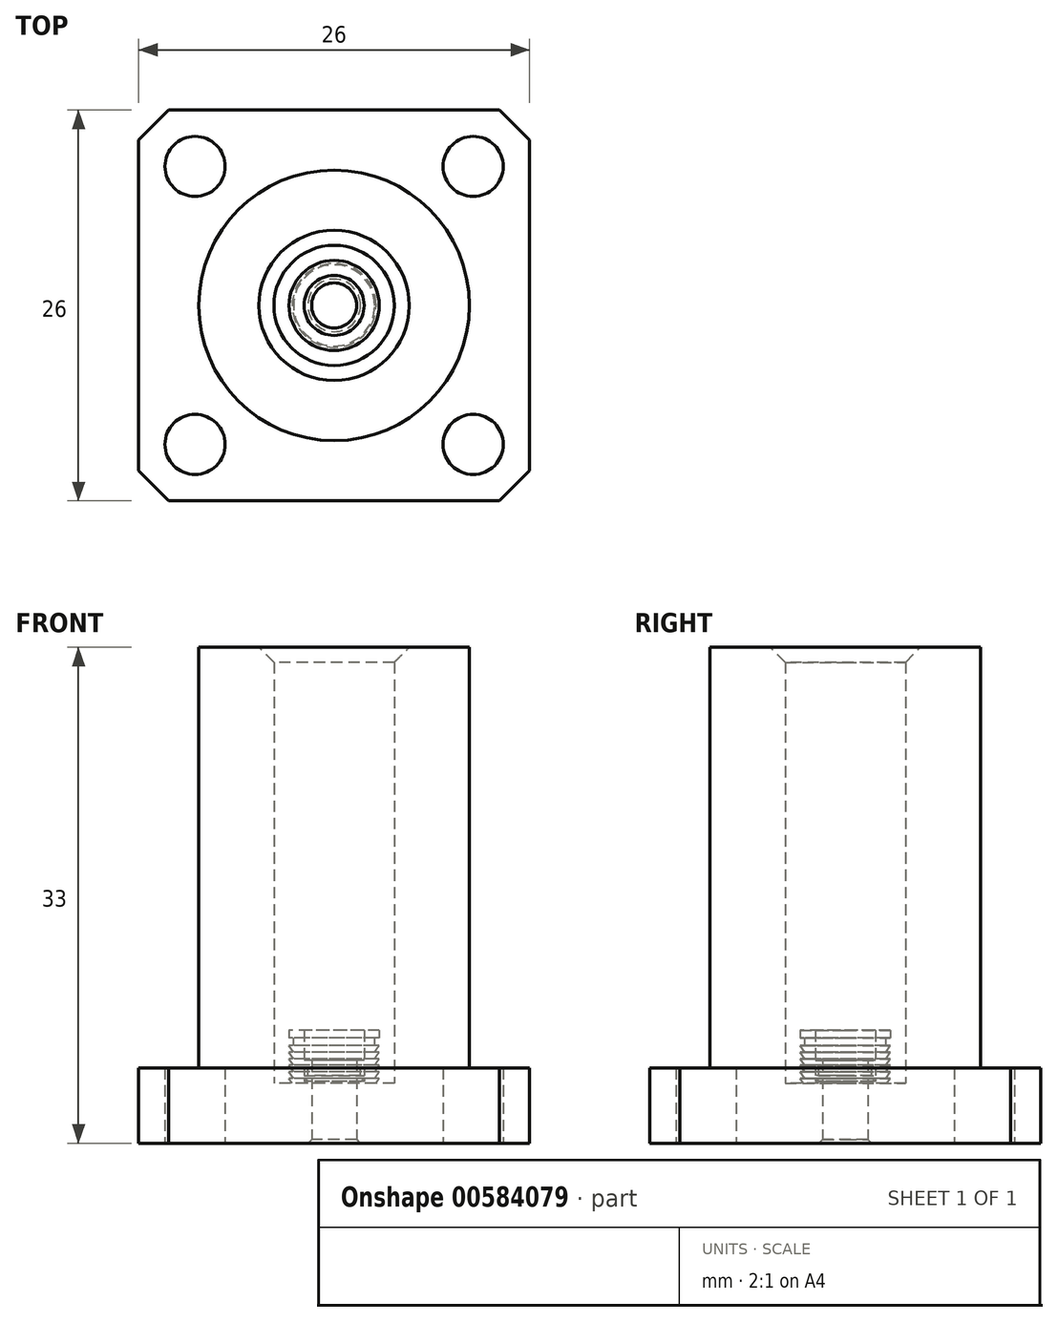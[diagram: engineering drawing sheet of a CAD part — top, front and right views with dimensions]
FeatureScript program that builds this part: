
annotation { "Feature Type Name" : "Feature", "Feature Type Description" : "" }
export const myFeature = defineFeature(function(context is Context, id is Id, definition is map)
    precondition{}
    {
        {
            var Q0;
            Q0=qCreatedBy(makeId("Top.planeOp"),FACE);
            var sketch = newSketch(context, id + "F0", { "sketchPlane" : qUnion([Q0])});
            skCircle(sketch, "E0", {"center": v(0, 0) * mm, "radius": 2.25 * mm});
            skCircle(sketch, "E1", {"center": v(0, 0) * mm, "radius": 1.5 * mm});
            skSolve(sketch);
        }
        {
            var Q0;
            Q0=makeQuery(id+"F0.imprint","IMPRINT",FACE,{"disambiguationData":[TD([[makeQuery(id+"F0.imprint","IMPRINT",EDGE,{"derivedFrom":sQuery(id+"F0.wireOp",EDGE,"E0")}),1.0]])]});
            extrude(context, id + "F1", {"entities" : qUnion([Q0]), "depth" : 5.5 * mm, "offsetDistance" : 25 * mm});
        }
        {
            var Q0;
            Q0=qCreatedBy(makeId("Front.planeOp"),FACE);
            var sketch = newSketch(context, id + "F2", { "sketchPlane" : qUnion([Q0])});
            skLineSegment(sketch, "E2", {"start": v(-2.25, 0) * mm, "end": v(-2.25, 5.5) * mm});
            skLineSegment(sketch, "E3", {"start": v(2.25, 5.5) * mm, "end": v(2.25, 0) * mm});
            skLineSegment(sketch, "E4", {"start": v(2.25, 5) * mm, "end": v(1.75, 5) * mm});
            skLineSegment(sketch, "E5", {"start": v(1.75, 5) * mm, "end": v(1.75, 4.5) * mm});
            skLineSegment(sketch, "E6", {"start": v(1.75, 4.5) * mm, "end": v(2.25, 4.5) * mm});
            skLineSegment(sketch, "E7", {"start": v(2.25, 4.5) * mm, "end": v(1.75, 4.1) * mm});
            skLineSegment(sketch, "E8", {"start": v(1.75, 4.1) * mm, "end": v(2.25, 4.1) * mm});
            skLineSegment(sketch, "E9", {"start": v(2.25, 4.1) * mm, "end": v(1.75, 3.7) * mm});
            skLineSegment(sketch, "E10", {"start": v(1.75, 3.7) * mm, "end": v(2.25, 3.7) * mm});
            skLineSegment(sketch, "E11", {"start": v(2.25, 3.7) * mm, "end": v(1.75, 3.3) * mm});
            skLineSegment(sketch, "E12", {"start": v(1.75, 3.3) * mm, "end": v(2.25, 3.3) * mm});
            skPoint(sketch, "E12.endSnap0", {"position": v(2.25, 2.75) * mm});
            skLineSegment(sketch, "E13", {"start": v(2.25, 3.3) * mm, "end": v(1.75, 2.9) * mm});
            skLineSegment(sketch, "E14", {"start": v(1.75, 2.9) * mm, "end": v(2.25, 2.9) * mm});
            skLineSegment(sketch, "E15", {"start": v(2.25, 2.9) * mm, "end": v(1.75, 2.5) * mm});
            skLineSegment(sketch, "E16", {"start": v(1.75, 2.5) * mm, "end": v(2.25, 2.5) * mm});
            skLineSegment(sketch, "E17", {"start": v(2.25, 2.5) * mm, "end": v(1.75, 2.1) * mm});
            skLineSegment(sketch, "E18", {"start": v(1.75, 2.1) * mm, "end": v(2.25, 2.1) * mm});
            skLineSegment(sketch, "E19", {"start": v(2.25, 2.1) * mm, "end": v(1.75, 1.7) * mm});
            skLineSegment(sketch, "E20", {"start": v(1.75, 1.7) * mm, "end": v(2.25, 1.7) * mm});
            skLineSegment(sketch, "E21", {"start": v(2.25, 1.7) * mm, "end": v(1.75, 1.3) * mm});
            skLineSegment(sketch, "E22", {"start": v(1.75, 1.3) * mm, "end": v(2.25, 1.3) * mm});
            skLineSegment(sketch, "E23", {"start": v(2.25, 1.3) * mm, "end": v(1.75, 0.9) * mm});
            skLineSegment(sketch, "E24", {"start": v(1.75, 0.9) * mm, "end": v(1.75, 0.6) * mm});
            skLineSegment(sketch, "E25", {"start": v(1.75, 0.6) * mm, "end": v(2.25, 0.6) * mm});
            skLineSegment(sketch, "E26", {"start": v(2.25, 0.3) * mm, "end": v(1.95, 0) * mm});
            skLineSegment(sketch, "E27", {"start": v(2.25, 5) * mm, "end": v(2.25, 0) * mm});
            skLineSegment(sketch, "E28", {"start": v(1.95, 0) * mm, "end": v(2.25, 0) * mm});
            skSolve(sketch);
        }
        {
            var Q0;
            {var subQ0=sQuery(id+"F2.wireOp",EDGE,"E4");Q0=makeQuery(id+"F2.imprint","IMPRINT",FACE,{"disambiguationData":[TD([[makeQuery(id+"F2.imprint","IMPRINT",EDGE,{"derivedFrom":subQ0}),1.0]])]});}
            var Q1;
            {var subQ0=sQuery(id+"F2.wireOp",EDGE,"E7");Q1=makeQuery(id+"F2.imprint","IMPRINT",FACE,{"disambiguationData":[TD([[makeQuery(id+"F2.imprint","IMPRINT",EDGE,{"derivedFrom":subQ0}),1.0]])]});}
            var Q2;
            {var subQ0=sQuery(id+"F2.wireOp",EDGE,"E9");Q2=makeQuery(id+"F2.imprint","IMPRINT",FACE,{"disambiguationData":[TD([[makeQuery(id+"F2.imprint","IMPRINT",EDGE,{"derivedFrom":subQ0}),1.0]])]});}
            var Q3;
            {var subQ0=sQuery(id+"F2.wireOp",EDGE,"E11");Q3=makeQuery(id+"F2.imprint","IMPRINT",FACE,{"disambiguationData":[TD([[makeQuery(id+"F2.imprint","IMPRINT",EDGE,{"derivedFrom":subQ0}),1.0]])]});}
            var Q4;
            {var subQ0=sQuery(id+"F2.wireOp",EDGE,"E13");Q4=makeQuery(id+"F2.imprint","IMPRINT",FACE,{"disambiguationData":[TD([[makeQuery(id+"F2.imprint","IMPRINT",EDGE,{"derivedFrom":subQ0}),1.0]])]});}
            var Q5;
            {var subQ0=sQuery(id+"F2.wireOp",EDGE,"E15");Q5=makeQuery(id+"F2.imprint","IMPRINT",FACE,{"disambiguationData":[TD([[makeQuery(id+"F2.imprint","IMPRINT",EDGE,{"derivedFrom":subQ0}),1.0]])]});}
            var Q6;
            {var subQ0=sQuery(id+"F2.wireOp",EDGE,"E17");Q6=makeQuery(id+"F2.imprint","IMPRINT",FACE,{"disambiguationData":[TD([[makeQuery(id+"F2.imprint","IMPRINT",EDGE,{"derivedFrom":subQ0}),1.0]])]});}
            var Q7;
            {var subQ0=sQuery(id+"F2.wireOp",EDGE,"E19");Q7=makeQuery(id+"F2.imprint","IMPRINT",FACE,{"disambiguationData":[TD([[makeQuery(id+"F2.imprint","IMPRINT",EDGE,{"derivedFrom":subQ0}),1.0]])]});}
            var Q8;
            {var subQ0=sQuery(id+"F2.wireOp",EDGE,"E21");Q8=makeQuery(id+"F2.imprint","IMPRINT",FACE,{"disambiguationData":[TD([[makeQuery(id+"F2.imprint","IMPRINT",EDGE,{"derivedFrom":subQ0}),1.0]])]});}
            var Q9;
            {var subQ0=sQuery(id+"F2.wireOp",EDGE,"E23");Q9=makeQuery(id+"F2.imprint","IMPRINT",FACE,{"disambiguationData":[TD([[makeQuery(id+"F2.imprint","IMPRINT",EDGE,{"derivedFrom":subQ0}),1.0]])]});}
            var Q10;
            {var subQ0=sQuery(id+"F2.wireOp",EDGE,"E26");Q10=makeQuery(id+"F2.imprint","IMPRINT",FACE,{"disambiguationData":[TD([[makeQuery(id+"F2.imprint","IMPRINT",EDGE,{"derivedFrom":subQ0}),1.0]])]});}
            var Q11;
            Q11=makeQuery(id+"F1.opExtrude","SWEPT_FACE",FACE,{"disambiguationData":[OSD([sQuery(id+"F0.wireOp",EDGE,"E1")])]});
            revolve(context, id + "F3", {"operationType" : NewBodyOperationType.REMOVE, "entities" : qUnion([Q0, Q1, Q2, Q3, Q4, Q5, Q6, Q7, Q8, Q9, Q10]), "axis" : qUnion([Q11]), "revolveType" : RevolveType.FULL, "oppositeDirection" : true});
        }
        {
            var Q0;
            Q0=qCreatedBy(makeId("Top.planeOp"),FACE);
            var sketch = newSketch(context, id + "F4", { "sketchPlane" : qUnion([Q0])});
            skCircle(sketch, "E29", {"center": v(0, 0) * mm, "radius": 3 * mm});
            skCircle(sketch, "E30", {"center": v(0, 0) * mm, "radius": 2 * mm});
            skSolve(sketch);
        }
        {
            var Q0;
            Q0=makeQuery(id+"F4.imprint","IMPRINT",FACE,{"disambiguationData":[TD([[makeQuery(id+"F4.imprint","IMPRINT",EDGE,{"derivedFrom":sQuery(id+"F4.wireOp",EDGE,"E29")}),1.0]])]});
            extrude(context, id + "F5", {"entities" : qUnion([Q0]), "depth" : 7.5 * mm, "offsetDistance" : 25 * mm});
        }
        {
            var Q0;
            Q0=qCreatedBy(makeId("Front.planeOp"),FACE);
            var sketch = newSketch(context, id + "F6", { "sketchPlane" : qUnion([Q0])});
            skLineSegment(sketch, "E31", {"start": v(-3, 0) * mm, "end": v(-3, 7.5) * mm});
            skLineSegment(sketch, "E32", {"start": v(3, 7.5) * mm, "end": v(3, 0) * mm});
            skLineSegment(sketch, "E33", {"start": v(3, 7.5) * mm, "end": v(3, 7) * mm});
            skLineSegment(sketch, "E34", {"start": v(3, 7) * mm, "end": v(2.7, 7) * mm});
            skLineSegment(sketch, "E35", {"start": v(2.7, 7) * mm, "end": v(2.7, 6.5) * mm});
            skLineSegment(sketch, "E36", {"start": v(2.7, 6.5) * mm, "end": v(3, 6.5) * mm});
            skLineSegment(sketch, "E37", {"start": v(3, 6.5) * mm, "end": v(2.7, 6.06) * mm});
            skLineSegment(sketch, "E38", {"start": v(2.7, 6.06) * mm, "end": v(3, 6.06) * mm});
            skLineSegment(sketch, "E39", {"start": v(3, 6.06) * mm, "end": v(2.7, 5.62) * mm});
            skLineSegment(sketch, "E40", {"start": v(2.7, 5.62) * mm, "end": v(3, 5.62) * mm});
            skLineSegment(sketch, "E41", {"start": v(3, 5.62) * mm, "end": v(2.7, 5.18) * mm});
            skLineSegment(sketch, "E42", {"start": v(2.7, 5.18) * mm, "end": v(3, 5.18) * mm});
            skLineSegment(sketch, "E43", {"start": v(3, 5.18) * mm, "end": v(2.7, 4.75) * mm});
            skLineSegment(sketch, "E44", {"start": v(2.7, 4.75) * mm, "end": v(3, 4.75) * mm});
            skLineSegment(sketch, "E45", {"start": v(3, 4.75) * mm, "end": v(2.7, 4.3) * mm});
            skLineSegment(sketch, "E46", {"start": v(2.7, 4.3) * mm, "end": v(3, 4.3) * mm});
            skLineSegment(sketch, "E47", {"start": v(3, 4.3) * mm, "end": v(2.7, 3.87) * mm});
            skLineSegment(sketch, "E48", {"start": v(2.7, 3.87) * mm, "end": v(3, 3.87) * mm});
            skLineSegment(sketch, "E49", {"start": v(3, 3.87) * mm, "end": v(2.7, 3.43) * mm});
            skLineSegment(sketch, "E50", {"start": v(2.7, 3.43) * mm, "end": v(3, 3.43) * mm});
            skLineSegment(sketch, "E51", {"start": v(3, 3.43) * mm, "end": v(2.7, 3) * mm});
            skLineSegment(sketch, "E52", {"start": v(2.7, 3) * mm, "end": v(3, 3) * mm});
            skLineSegment(sketch, "E53", {"start": v(3, 3) * mm, "end": v(2.7, 2.55) * mm});
            skLineSegment(sketch, "E54", {"start": v(2.7, 2.55) * mm, "end": v(3, 2.55) * mm});
            skLineSegment(sketch, "E55", {"start": v(3, 2.55) * mm, "end": v(2.7, 2.12) * mm});
            skLineSegment(sketch, "E56", {"start": v(2.7, 2.12) * mm, "end": v(3, 2.12) * mm});
            skLineSegment(sketch, "E57", {"start": v(3, 2.12) * mm, "end": v(2.7, 1.68) * mm});
            skLineSegment(sketch, "E58", {"start": v(2.7, 1.68) * mm, "end": v(3, 1.68) * mm});
            skLineSegment(sketch, "E59", {"start": v(3, 1.68) * mm, "end": v(2.7, 1.24) * mm});
            skLineSegment(sketch, "E60", {"start": v(2.7, 1.24) * mm, "end": v(3, 1.24) * mm});
            skLineSegment(sketch, "E61", {"start": v(3, 1.24) * mm, "end": v(2.7, 0.8) * mm});
            skLineSegment(sketch, "E62", {"start": v(2.7, 0.8) * mm, "end": v(2.7, 0.5) * mm});
            skLineSegment(sketch, "E63", {"start": v(2.7, 0.5) * mm, "end": v(3, 0.5) * mm});
            skLineSegment(sketch, "E64", {"start": v(3, 0.3) * mm, "end": v(2.7, 0) * mm});
            skLineSegment(sketch, "E65", {"start": v(2.7, 0) * mm, "end": v(3, 0) * mm});
            skLineSegment(sketch, "E66", {"start": v(3, 0.3) * mm, "end": v(3, 0) * mm});
            skSolve(sketch);
        }
        {
            var Q0;
            {var subQ0=sQuery(id+"F6.wireOp",EDGE,"E34");Q0=makeQuery(id+"F6.imprint","IMPRINT",FACE,{"disambiguationData":[TD([[makeQuery(id+"F6.imprint","IMPRINT",EDGE,{"derivedFrom":subQ0}),1.0]])]});}
            var Q1;
            {var subQ0=sQuery(id+"F6.wireOp",EDGE,"E37");Q1=makeQuery(id+"F6.imprint","IMPRINT",FACE,{"disambiguationData":[TD([[makeQuery(id+"F6.imprint","IMPRINT",EDGE,{"derivedFrom":subQ0}),1.0]])]});}
            var Q2;
            {var subQ0=sQuery(id+"F6.wireOp",EDGE,"E39");Q2=makeQuery(id+"F6.imprint","IMPRINT",FACE,{"disambiguationData":[TD([[makeQuery(id+"F6.imprint","IMPRINT",EDGE,{"derivedFrom":subQ0}),1.0]])]});}
            var Q3;
            {var subQ0=sQuery(id+"F6.wireOp",EDGE,"E41");Q3=makeQuery(id+"F6.imprint","IMPRINT",FACE,{"disambiguationData":[TD([[makeQuery(id+"F6.imprint","IMPRINT",EDGE,{"derivedFrom":subQ0}),1.0]])]});}
            var Q4;
            {var subQ0=sQuery(id+"F6.wireOp",EDGE,"E43");Q4=makeQuery(id+"F6.imprint","IMPRINT",FACE,{"disambiguationData":[TD([[makeQuery(id+"F6.imprint","IMPRINT",EDGE,{"derivedFrom":subQ0}),1.0]])]});}
            var Q5;
            {var subQ0=sQuery(id+"F6.wireOp",EDGE,"E45");Q5=makeQuery(id+"F6.imprint","IMPRINT",FACE,{"disambiguationData":[TD([[makeQuery(id+"F6.imprint","IMPRINT",EDGE,{"derivedFrom":subQ0}),1.0]])]});}
            var Q6;
            {var subQ0=sQuery(id+"F6.wireOp",EDGE,"E47");Q6=makeQuery(id+"F6.imprint","IMPRINT",FACE,{"disambiguationData":[TD([[makeQuery(id+"F6.imprint","IMPRINT",EDGE,{"derivedFrom":subQ0}),1.0]])]});}
            var Q7;
            {var subQ0=sQuery(id+"F6.wireOp",EDGE,"E49");Q7=makeQuery(id+"F6.imprint","IMPRINT",FACE,{"disambiguationData":[TD([[makeQuery(id+"F6.imprint","IMPRINT",EDGE,{"derivedFrom":subQ0}),1.0]])]});}
            var Q8;
            {var subQ0=sQuery(id+"F6.wireOp",EDGE,"E53");Q8=makeQuery(id+"F6.imprint","IMPRINT",FACE,{"disambiguationData":[TD([[makeQuery(id+"F6.imprint","IMPRINT",EDGE,{"derivedFrom":subQ0}),1.0]])]});}
            var Q9;
            {var subQ0=sQuery(id+"F6.wireOp",EDGE,"E51");Q9=makeQuery(id+"F6.imprint","IMPRINT",FACE,{"disambiguationData":[TD([[makeQuery(id+"F6.imprint","IMPRINT",EDGE,{"derivedFrom":subQ0}),1.0]])]});}
            var Q10;
            {var subQ0=sQuery(id+"F6.wireOp",EDGE,"E55");Q10=makeQuery(id+"F6.imprint","IMPRINT",FACE,{"disambiguationData":[TD([[makeQuery(id+"F6.imprint","IMPRINT",EDGE,{"derivedFrom":subQ0}),1.0]])]});}
            var Q11;
            {var subQ0=sQuery(id+"F6.wireOp",EDGE,"E57");Q11=makeQuery(id+"F6.imprint","IMPRINT",FACE,{"disambiguationData":[TD([[makeQuery(id+"F6.imprint","IMPRINT",EDGE,{"derivedFrom":subQ0}),1.0]])]});}
            var Q12;
            {var subQ0=sQuery(id+"F6.wireOp",EDGE,"E59");Q12=makeQuery(id+"F6.imprint","IMPRINT",FACE,{"disambiguationData":[TD([[makeQuery(id+"F6.imprint","IMPRINT",EDGE,{"derivedFrom":subQ0}),1.0]])]});}
            var Q13;
            {var subQ0=sQuery(id+"F6.wireOp",EDGE,"E61");Q13=makeQuery(id+"F6.imprint","IMPRINT",FACE,{"disambiguationData":[TD([[makeQuery(id+"F6.imprint","IMPRINT",EDGE,{"derivedFrom":subQ0}),1.0]])]});}
            var Q14;
            Q14=makeQuery(id+"F6.imprint","IMPRINT",FACE,{"disambiguationData":[TD([[makeQuery(id+"F6.imprint","IMPRINT",EDGE,{"derivedFrom":sQuery(id+"F6.wireOp",EDGE,"E64")}),1.0]])]});
            var Q15;
            Q15=makeQuery(id+"F5.opExtrude","SWEPT_FACE",FACE,{"disambiguationData":[OSD([sQuery(id+"F4.wireOp",EDGE,"E30")])]});
            revolve(context, id + "F7", {"operationType" : NewBodyOperationType.REMOVE, "entities" : qUnion([Q0, Q1, Q2, Q3, Q4, Q5, Q6, Q7, Q8, Q9, Q10, Q11, Q12, Q13, Q14]), "axis" : qUnion([Q15]), "revolveType" : RevolveType.FULL, "oppositeDirection" : true});
        }
        {
            var Q0;
            Q0=qCreatedBy(makeId("Top.planeOp"),FACE);
            var sketch = newSketch(context, id + "F8", { "sketchPlane" : qUnion([Q0])});
            skLineSegment(sketch, "E67.bottom", {"start": v(13, -13) * mm, "end": v(-13, -13) * mm});
            skLineSegment(sketch, "E67.top", {"start": v(13, 13) * mm, "end": v(-13, 13) * mm});
            skLineSegment(sketch, "E67.left", {"start": v(13, -13) * mm, "end": v(13, 13) * mm});
            skLineSegment(sketch, "E67.right", {"start": v(-13, -13) * mm, "end": v(-13, 13) * mm});
            skPoint(sketch, "E67.middle", {"position": v(0, 0) * mm});
            skCircle(sketch, "E68", {"center": v(0, 0) * mm, "radius": 4 * mm});
            skCircle(sketch, "E69", {"center": v(-9.25, 9.25) * mm, "radius": 2 * mm});
            skCircle(sketch, "E70", {"center": v(9.25, 9.25) * mm, "radius": 2 * mm});
            skCircle(sketch, "E71", {"center": v(9.25, -9.25) * mm, "radius": 2 * mm});
            skCircle(sketch, "E72", {"center": v(-9.25, -9.25) * mm, "radius": 2 * mm});
            skLineSegment(sketch, "E73", {"start": v(0, 0) * mm, "end": v(13, 0) * mm, "construction": true});
            skLineSegment(sketch, "E74", {"start": v(0, 0) * mm, "end": v(0, 13) * mm, "construction": true});
            skSolve(sketch);
        }
        {
            var Q0;
            Q0=makeQuery(id+"F8.imprint","IMPRINT",FACE,{"disambiguationData":[TD([[makeQuery(id+"F8.imprint","IMPRINT",EDGE,{"derivedFrom":sQuery(id+"F8.wireOp",EDGE,"E67.bottom")}),-1.0]])]});
            extrude(context, id + "F9", {"entities" : qUnion([Q0]), "depth" : 5 * mm, "offsetDistance" : 25 * mm});
        }
        {
            var Q0;
            Q0=makeQuery(id+"F9.opExtrude","CAP_FACE",FACE,{"disambiguationData":[OSD([sQuery(id+"F8.wireOp",EDGE,"E67.bottom"),sQuery(id+"F8.wireOp",EDGE,"E67.top"),sQuery(id+"F8.wireOp",EDGE,"E67.left"),sQuery(id+"F8.wireOp",EDGE,"E67.right"),sQuery(id+"F8.wireOp",EDGE,"E68"),sQuery(id+"F8.wireOp",EDGE,"E69"),sQuery(id+"F8.wireOp",EDGE,"E70"),sQuery(id+"F8.wireOp",EDGE,"E71"),sQuery(id+"F8.wireOp",EDGE,"E72")])],"isStart":false});
            var sketch = newSketch(context, id + "F10", { "sketchPlane" : qUnion([Q0])});
            skCircle(sketch, "E75", {"center": v(0, 0) * mm, "radius": 9 * mm});
            skSolve(sketch);
        }
        {
            var Q0;
            Q0=makeQuery(id+"F10.imprint","IMPRINT",FACE,{"disambiguationData":[TD([[makeQuery(id+"F10.imprint","IMPRINT",EDGE,{"derivedFrom":sQuery(id+"F10.wireOp",EDGE,"E75")}),1.0]])]});
            extrude(context, id + "F11", {"entities" : qUnion([Q0]), "operationType" : NewBodyOperationType.ADD, "depth" : (33 - 5) * mm, "offsetDistance" : 25 * mm});
        }
        {
            var Q0;
            Q0=makeQuery(id+"F9.opExtrude","SWEPT_EDGE",EDGE,{"disambiguationData":[OSD([sQuery(id+"F8.wireOp",EDGE,"E67.bottom"),sQuery(id+"F8.wireOp",EDGE,"E67.right")])]});
            var Q1;
            Q1=makeQuery(id+"F9.opExtrude","SWEPT_EDGE",EDGE,{"disambiguationData":[OSD([sQuery(id+"F8.wireOp",EDGE,"E67.bottom"),sQuery(id+"F8.wireOp",EDGE,"E67.left")])]});
            var Q2;
            Q2=makeQuery(id+"F9.opExtrude","SWEPT_EDGE",EDGE,{"disambiguationData":[OSD([sQuery(id+"F8.wireOp",EDGE,"E67.top"),sQuery(id+"F8.wireOp",EDGE,"E67.left")])]});
            var Q3;
            Q3=makeQuery(id+"F9.opExtrude","SWEPT_EDGE",EDGE,{"disambiguationData":[OSD([sQuery(id+"F8.wireOp",EDGE,"E67.top"),sQuery(id+"F8.wireOp",EDGE,"E67.right")])]});
            chamfer(context, id + "F12", {"entities" : qUnion([Q0, Q1, Q2, Q3]), "width" : 2 * mm, "tangentPropagation" : true});
        }
        {
            var Q0;
            Q0=makeQuery(id+"F11.opExtrude","CAP_EDGE",EDGE,{"disambiguationData":[OSD([sQuery(id+"F8.wireOp",EDGE,"E68")])],"isStart":false});
            var Q1;
            Q1=makeQuery(id+"F9.opExtrude","CAP_EDGE",EDGE,{"disambiguationData":[OSD([sQuery(id+"F8.wireOp",EDGE,"E68")])],"isStart":true});
            chamfer(context, id + "F13", {"entities" : qUnion([Q0, Q1]), "width" : 1 * mm, "tangentPropagation" : true});
        }
        {
            var Q0;
            Q0=qCreatedBy(makeId("Top.planeOp"),FACE);
            var sketch = newSketch(context, id + "F14", { "sketchPlane" : qUnion([Q0])});
            skCircle(sketch, "E76", {"center": v(0, 0) * mm, "radius": 5.75 * mm});
            skSolve(sketch);
        }
        {
            var Q0;
            Q0=makeQuery(id+"F14.imprint","IMPRINT",FACE,{"disambiguationData":[TD([[makeQuery(id+"F14.imprint","IMPRINT",EDGE,{"derivedFrom":sQuery(id+"F14.wireOp",EDGE,"E76")}),1.0]])]});
            extrude(context, id + "F15", {"entities" : qUnion([Q0]), "depth" : 1 * mm, "offsetDistance" : 25 * mm});
        }
        {
            var Q0;
            Q0=makeQuery(id+"F15.opExtrude","CAP_FACE",FACE,{"disambiguationData":[OSD([sQuery(id+"F14.wireOp",EDGE,"E76")])],"isStart":false});
            var sketch = newSketch(context, id + "F16", { "sketchPlane" : qUnion([Q0])});
            skCircle(sketch, "E77", {"center": v(0, 0) * mm, "radius": 5 * mm});
            skSolve(sketch);
        }
        {
            var Q0;
            Q0=makeQuery(id+"F16.imprint","IMPRINT",FACE,{"disambiguationData":[TD([[makeQuery(id+"F16.imprint","IMPRINT",EDGE,{"derivedFrom":sQuery(id+"F16.wireOp",EDGE,"E77")}),1.0]])]});
            extrude(context, id + "F17", {"entities" : qUnion([Q0]), "operationType" : NewBodyOperationType.ADD, "depth" : 3 * mm, "offsetDistance" : 25 * mm});
        }
        {
            var Q0;
            Q0=makeQuery(id+"F17.opExtrude","CAP_FACE",FACE,{"disambiguationData":[OSD([sQuery(id+"F16.wireOp",EDGE,"E77")])],"isStart":false});
            var sketch = newSketch(context, id + "F18", { "sketchPlane" : qUnion([Q0])});
            skCircle(sketch, "E78", {"center": v(0, 0) * mm, "radius": 1.5 * mm});
            skSolve(sketch);
        }
        {
            var Q0;
            Q0=makeQuery(id+"F18.imprint","IMPRINT",FACE,{"disambiguationData":[TD([[makeQuery(id+"F18.imprint","IMPRINT",EDGE,{"derivedFrom":sQuery(id+"F18.wireOp",EDGE,"E78")}),1.0]])]});
            extrude(context, id + "F19", {"entities" : qUnion([Q0]), "operationType" : NewBodyOperationType.REMOVE, "endBound" : BoundingType.THROUGH_ALL, "oppositeDirection" : true, "depth" : 25 * mm, "offsetDistance" : 25 * mm});
        }
        {
            var Q0;
            Q0=makeQuery(id+"F17.opExtrude","CAP_EDGE",EDGE,{"disambiguationData":[OSD([sQuery(id+"F16.wireOp",EDGE,"E77")])],"isStart":false});
            var Q1;
            Q1=makeQuery(id+"F19.boolean.opBoolean","COPY",EDGE,{"derivedFrom":makeQuery(id+"F19.opExtrude","CAP_EDGE",EDGE,{"disambiguationData":[OSD([sQuery(id+"F18.wireOp",EDGE,"E78")])],"isStart":true})});
            var Q2;
            Q2=makeQuery(id+"F15.opExtrude","CAP_EDGE",EDGE,{"disambiguationData":[OSD([sQuery(id+"F14.wireOp",EDGE,"E76")])],"isStart":false});
            var Q3;
            Q3=makeQuery(id+"F15.opExtrude","CAP_EDGE",EDGE,{"disambiguationData":[OSD([sQuery(id+"F14.wireOp",EDGE,"E76")])],"isStart":true});
            var Q4;
            Q4=makeQuery(id+"F19.boolean.opBoolean","INTERSECT",EDGE,{"derivedFrom":[makeQuery(id+"F15.opExtrude","CAP_FACE",FACE,{"disambiguationData":[OSD([sQuery(id+"F14.wireOp",EDGE,"E76")])],"isStart":true}),makeQuery(id+"F19.opExtrude","SWEPT_FACE",FACE,{"disambiguationData":[OSD([sQuery(id+"F18.wireOp",EDGE,"E78")])]})]});
            chamfer(context, id + "F20", {"entities" : qUnion([Q0, Q1, Q2, Q3, Q4]), "width" : 0.25 * mm, "tangentPropagation" : true});
        }
    });
